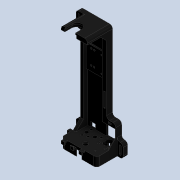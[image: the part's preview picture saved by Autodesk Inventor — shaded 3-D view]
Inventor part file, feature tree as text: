
AUTODESK INVENTOR PART (.ipt)
format: ipt  version: 2020 (Build 240168000, 168)  size: 855,040 bytes
history: native  units: mm
features: extrude x27, sketch x27, chamfer x4, fillet x4, hole x2, pattern_linear x2, direct_edit x2, move_body x2, projected_geometry x1
ambient origin geometry x8: Origin, YZ Plane, XZ Plane, XY Plane, X Axis, Y Axis, Z Axis, Center Point
bodies: Solid1 (feature_tree)
feature tree (71):
  extrude  "Extrusion1"  Depth=120.0mm
  extrude  "Extrusion2"  Depth=10.0mm
  extrude  "Extrusion3"  Depth=22.0mm
  extrude  "Extrusion4"  Depth=31.0mm
  chamfer  "Chamfer1"  [1 undecoded]
  extrude  "Extrusion16"  TaperAngle=0.0deg  [1 undecoded]
  chamfer  "Chamfer2"  Distance=20.0mm Angle=45.0deg
  hole  "Hole1"  [1 undecoded]
  extrude  "Extrusion17"  Depth=40.0mm
  extrude  "Extrusion18"  Depth=31.0mm
  extrude  "Extrusion19"  Depth=4.0mm
  hole  "Hole3"  [1 undecoded]
  extrude  "Extrusion20"  Depth=44.0mm
  extrude  "Extrusion21"  TaperAngle=0.0deg  [1 undecoded]
  extrude  "Extrusion22"  Depth=45.0mm
  chamfer  "Chamfer6"  Distance=2.0mm
  extrude  "Extrusion23"  Depth=5.0mm
  extrude  "Extrusion24"  Depth=10.0mm
  fillet  "Fillet2"  Radius=9.0mm
  extrude  "Extrusion25"  Depth=5.0mm TaperAngle=0.0deg
  extrude  "Extrusion26"  Depth=17.0mm
  extrude  "Extrusion27"  Depth=15.0mm
  fillet  "Fillet3"  Radius=5.0mm
  extrude  "Extrusion28"  Depth=5.0mm
  extrude  "Extrusion29"  Depth=5.0mm
  fillet  "Fillet5"  Radius=5.0mm
  extrude  "Extrusion30"  Depth=45.0mm
  extrude  "Extrusion31"  Depth=5.0mm
  pattern_linear  "Rectangular Pattern1"  Spacing1=1.5mm  [1 undecoded]
  pattern_linear  "Rectangular Pattern2"  Spacing1=6.0mm  [1 undecoded]
  extrude  "Extrusion32"  Depth=6.0mm
  extrude  "Extrusion33"  Depth=16.0mm TaperAngle=0.0deg
  extrude  "Extrusion34"  Depth=0.5mm
  fillet  "Fillet6"  Radius=5.0mm
  extrude  "Extrusion36"  Depth=5.0mm
  extrude  "Extrusion37"  Depth=6.0mm
  extrude  "Extrusion38"  Depth=6.0mm
  extrude  "Extrusion39"  Depth=12.0mm
  chamfer  "Chamfer8"  Distance=18.0mm
  direct_edit  "Direct Edit1"
  direct_edit  "Direct Edit2"
  sketch  "Sketch1"  dims[d0=340.0mm d1=120.0mm]
  sketch  "Sketch2"  dims[d2=85.0mm d3=0.0mm d5=10.0mm]
  sketch  "Sketch3"  dims[d6=75.0mm d7=0.0mm d8=22.0mm]
  sketch  "Sketch4"  dims[d10=31.0mm d11=0.6mm d12=0.0mm d13=0.0mm]
  sketch  "Sketch17"  dims[d14=20.0mm d17=0.0mm d18=0.0mm d19=20.0mm d20=2.0mm d21=45.0deg]
  sketch  "Sketch18"  dims[d22=5.0mm d23=2.0mm d24=45.0deg d112=15.0mm]
  sketch  "Sketch22"  dims[d116=32.0mm d117=40.0mm]
  sketch  "Sketch24"  dims[d118=10.0mm d119=0.0mm]
  sketch  "Sketch25"  dims[d120=13.0mm d121=6.0mm d122=16.3mm d123=8.0mm d124=90.0deg d125=8.0mm d126=20.594885mm d134=31.0mm]
  sketch  "Sketch26"  dims[d135=2.5mm d136=4.0mm]
  sketch  "Sketch27"  dims[d137=5.0mm d138=23.0mm]
  sketch  "Sketch28"  dims[d139=10.0mm d140=0.0mm d141=44.0mm]
  sketch  "Sketch29"  dims[d142=45.0mm d143=0.0mm d144=0.0mm]
  sketch  "Sketch30"  dims[d145=2.0mm d146=45.0mm d147=2.0mm d148=0.0mm]
  sketch  "Sketch32"  dims[d151=10.0mm d157=5.0mm]
  sketch  "Sketch33"  dims[d158=5.0mm d159=10.0mm]
  sketch  "Sketch34"  dims[d160=3.0mm d161=6.0mm d162=8.0mm d163=5.0mm d164=90.0deg d165=3.0mm d166=0.0mm d167=9.0mm]
  sketch  "Sketch35"  dims[d168=9.0mm d169=5.0mm d170=0.0mm]
  sketch  "Sketch36"  dims[d171=15.0mm d172=17.0mm]
  sketch  "Sketch37"  dims[d173=0.0mm d174=0.0mm d175=15.0mm d176=5.0mm d177=0.0mm]
  sketch  "Sketch38"  dims[d178=20.0mm d179=2.0mm d180=45.0deg d181=5.0mm]
  sketch  "Sketch39"  dims[d182=5.0mm d183=5.0mm d184=5.0mm]
  sketch  "Sketch40"  dims[d185=2.5mm d186=45.0mm]
  sketch  "Sketch42"  dims[d187=5.0mm d188=5.0mm]
  sketch  "Sketch43"  dims[d189=5.0mm]
  sketch  "Sketch45"  dims[d190=21.0mm d191=0.0mm]
  sketch  "Sketch46"  dims[d192=45.0mm d193=1.5mm d194=6.0mm d195=6.0mm d196=16.0mm d197=0.0mm d198=0.5mm d199=5.0mm d200=5.0mm d201=6.0mm d202=6.0mm d203=12.0mm d204=18.0mm d205=0.0mm d206=2.5mm d207=45.0mm d208=45.0mm d209=20.0mm d210=20.0mm d211=15.0mm d212=0.0mm d213=6.0mm d214=10.0mm d216=10.0mm d217=0.0mm d218=0.0mm d219=10.0mm d221=20.0mm d222=50.0mm d224=10.0mm d225=10.0mm d226=0.0mm d227=0.0mm d228=5.0mm d229=10.0mm d230=15.0mm d231=5.0mm d232=5.0mm d233=5.0mm d234=50.0mm d236=10.0mm d237=0.0mm d238=10.0mm d239=28.0mm d241=40.0mm d242=10.0mm d243=10.0mm d244=10.0mm d245=0.0mm d248=40.0mm d249=0.0mm d250=20.0mm d252=60.0mm d253=20.0mm d255=30.0mm d256=3.0mm d257=4.0mm d258=10.0mm d259=0.0mm d260=10.0mm d261=10.0mm d262=30.0mm d263=10.0mm d264=0.0mm d265=3.0mm d267=10.0mm d268=0.0mm d269=4.0mm d280=10.0mm d281=21.5mm d282=0.0mm d283=47.553mm d284=25.546mm d285=26.901mm d286=5.0mm d287=5.0mm d288=21.5mm d289=0.0mm d293=12.0mm d294=21.5mm d295=0.0mm d296=10.0mm d297=10.0mm d298=5.0mm d299=0.0mm d300=5.0mm d301=2.0mm d302=45.0deg d303=0.0mm d304=0.0mm d305=-5.0mm d306=5.0mm d307=0.0mm d308=0.0mm d309=-3.0mm d310=5.0mm d311=4.0mm d312=3.0mm d313=5.0mm]
  projected_geometry  "Projected Loop1"
  move_body  "Move1"
  move_body  "Move2"
note: 7 required parameter values undecoded (feature->parameter linkage not recoverable at this tier; creation-order binding heuristic only, values carry confidence <= 0.55)
